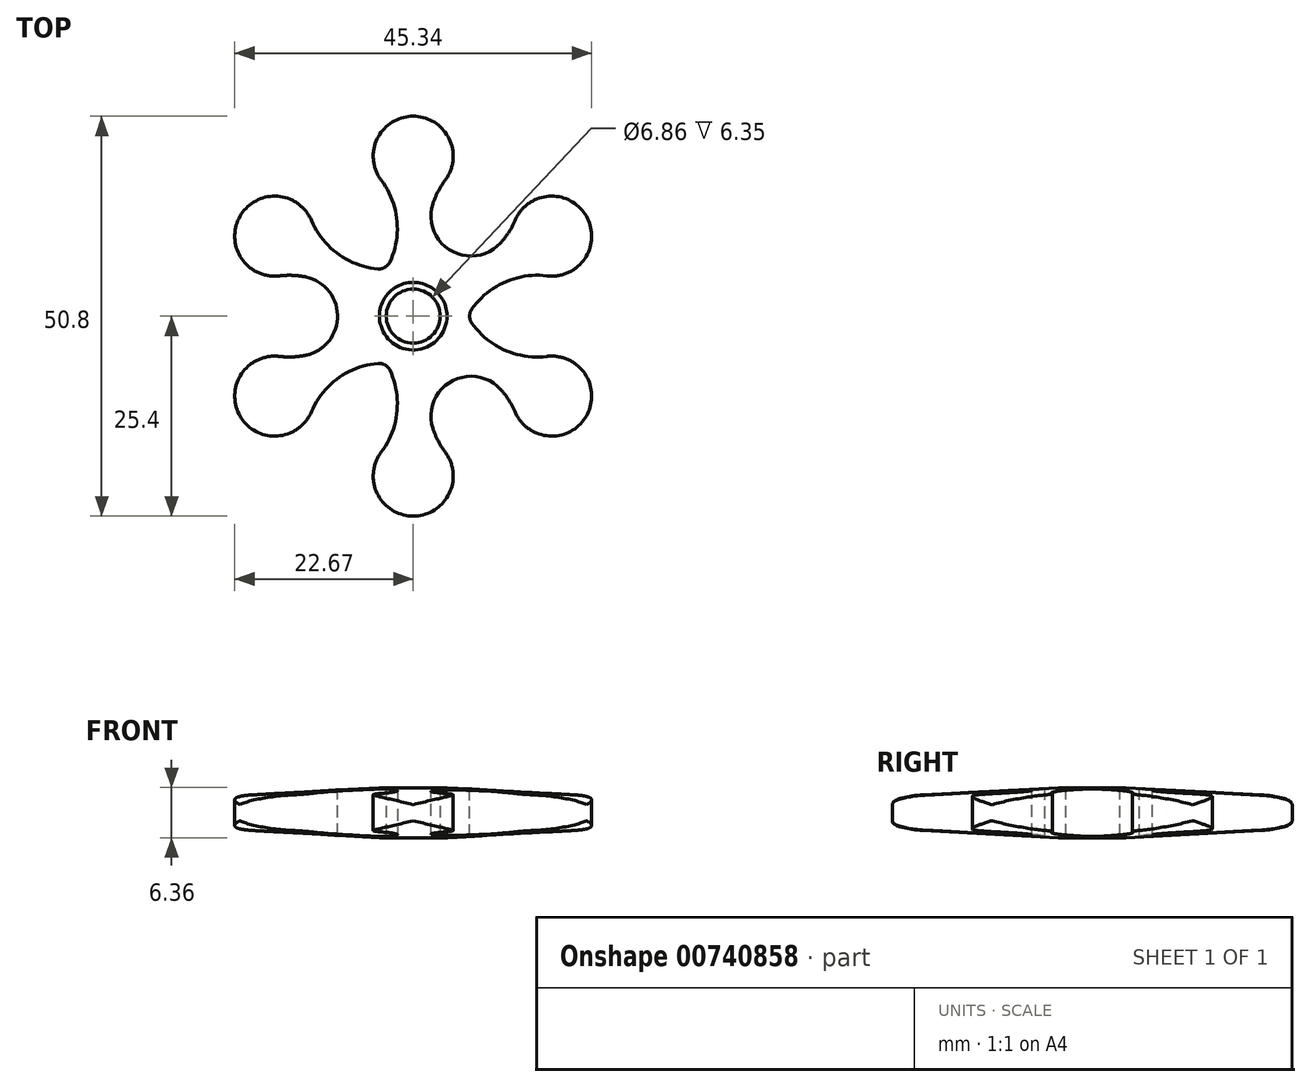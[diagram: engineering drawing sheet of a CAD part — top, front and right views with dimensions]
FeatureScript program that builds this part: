
annotation { "Feature Type Name" : "Feature", "Feature Type Description" : "" }
export const myFeature = defineFeature(function(context is Context, id is Id, definition is map)
    precondition{}
    {
        {
            var Q0;
            Q0=qCreatedBy(makeId("Top.planeOp"),FACE);
            var sketch = newSketch(context, id + "F0", { "sketchPlane" : qUnion([Q0])});
            skCircle(sketch, "E0", {"center": v(0, 0) * mm, "radius": 3.43 * mm});
            skCircle(sketch, "E1", {"center": v(0, 0) * mm, "radius": 25.4 * mm, "construction": true});
            skLineSegment(sketch, "E2", {"start": v(0, 0) * mm, "end": v(0, 25.4) * mm, "construction": true});
            skArc(sketch, "E3", {"start": v(4.06, 17.26) * mm, "mid": v(0, 25.4) * mm, "end": v(-4.06, 17.26) * mm});
            skArc(sketch, "E4", {"start": v(-4.68, 4.29) * mm, "mid": v(0, -6.35) * mm, "end": v(4.68, 4.29) * mm});
            skArc(sketch, "E5", {"start": v(-4.68, 4.29) * mm, "mid": v(-2.03, 10.66) * mm, "end": v(-4.06, 17.26) * mm});
            skPoint(sketch, "E5.first.point", {"position": v(-4.06, 17.26) * mm});
            skPoint(sketch, "E5.second.point", {"position": v(-4.68, 4.29) * mm});
            skArc(sketch, "E6", {"start": v(4.06, 17.26) * mm, "mid": v(2.03, 10.66) * mm, "end": v(4.68, 4.29) * mm});
            skPoint(sketch, "E6.first.point", {"position": v(4.06, 17.26) * mm});
            skPoint(sketch, "E6.second.point", {"position": v(4.68, 4.29) * mm});
            skArc(sketch, "E7.1.0", {"start": v(-12.92, 12.15) * mm, "mid": v(-8.22, 7.09) * mm, "end": v(-1.37, 6.2) * mm});
            skArc(sketch, "E7.1.1", {"start": v(-6.06, -1.91) * mm, "mid": v(-10.25, 3.58) * mm, "end": v(-16.98, 5.12) * mm});
            skArc(sketch, "E7.1.2", {"start": v(-12.92, 12.15) * mm, "mid": v(-22, 12.7) * mm, "end": v(-16.98, 5.12) * mm});
            skArc(sketch, "E7.2.0", {"start": v(-16.98, -5.12) * mm, "mid": v(-10.25, -3.58) * mm, "end": v(-6.06, 1.91) * mm});
            skArc(sketch, "E7.2.1", {"start": v(-1.37, -6.2) * mm, "mid": v(-8.22, -7.09) * mm, "end": v(-12.92, -12.15) * mm});
            skArc(sketch, "E7.2.2", {"start": v(-16.98, -5.12) * mm, "mid": v(-22, -12.7) * mm, "end": v(-12.92, -12.15) * mm});
            skLineSegment(sketch, "E8", {"start": v(0, 0) * mm, "end": v(-22, -12.7) * mm, "construction": true});
            skLineSegment(sketch, "E9", {"start": v(0, 0) * mm, "end": v(22, -12.7) * mm, "construction": true});
            skArc(sketch, "E10.4.3.0", {"start": v(4.68, -4.29) * mm, "mid": v(2.03, -10.66) * mm, "end": v(4.06, -17.26) * mm});
            skArc(sketch, "E10.5.3.0", {"start": v(-4.06, -17.26) * mm, "mid": v(-2.03, -10.66) * mm, "end": v(-4.68, -4.29) * mm});
            skArc(sketch, "E10.8.3.0", {"start": v(-4.06, -17.26) * mm, "mid": v(0, -25.4) * mm, "end": v(4.06, -17.26) * mm});
            skArc(sketch, "E10.4.4.0", {"start": v(6.06, 1.91) * mm, "mid": v(10.25, -3.58) * mm, "end": v(16.98, -5.12) * mm});
            skArc(sketch, "E10.5.4.0", {"start": v(12.92, -12.15) * mm, "mid": v(8.22, -7.09) * mm, "end": v(1.37, -6.2) * mm});
            skArc(sketch, "E10.8.4.0", {"start": v(12.92, -12.15) * mm, "mid": v(22, -12.7) * mm, "end": v(16.98, -5.12) * mm});
            skArc(sketch, "E10.4.5.0", {"start": v(1.37, 6.2) * mm, "mid": v(8.22, 7.09) * mm, "end": v(12.92, 12.15) * mm});
            skArc(sketch, "E10.5.5.0", {"start": v(16.98, 5.12) * mm, "mid": v(10.25, 3.58) * mm, "end": v(6.06, -1.91) * mm});
            skArc(sketch, "E10.8.5.0", {"start": v(16.98, 5.12) * mm, "mid": v(22, 12.7) * mm, "end": v(12.92, 12.15) * mm});
            skSolve(sketch);
        }
        {
            var Q0;
            {var subQ0=sQuery(id+"F0.wireOp",EDGE,"E7.1.0");Q0=makeQuery(id+"F0.imprint","IMPRINT",FACE,{"disambiguationData":[TD([[makeQuery(id+"F0.imprint","IMPRINT",EDGE,{"derivedFrom":subQ0}),-1.0]])]});}
            var Q1;
            {var subQ0=sQuery(id+"F0.wireOp",EDGE,"E10.8.5.0");Q1=makeQuery(id+"F0.imprint","IMPRINT",FACE,{"disambiguationData":[TD([[makeQuery(id+"F0.imprint","IMPRINT",EDGE,{"derivedFrom":subQ0}),1.0]])]});}
            var Q2;
            {var subQ0=sQuery(id+"F0.wireOp",EDGE,"E10.8.4.0");Q2=makeQuery(id+"F0.imprint","IMPRINT",FACE,{"disambiguationData":[TD([[makeQuery(id+"F0.imprint","IMPRINT",EDGE,{"derivedFrom":subQ0}),1.0]])]});}
            var Q3;
            {var subQ0=sQuery(id+"F0.wireOp",EDGE,"E10.8.3.0");Q3=makeQuery(id+"F0.imprint","IMPRINT",FACE,{"disambiguationData":[TD([[makeQuery(id+"F0.imprint","IMPRINT",EDGE,{"derivedFrom":subQ0}),1.0]])]});}
            var Q4;
            {var subQ0=sQuery(id+"F0.wireOp",EDGE,"E7.2.2");Q4=makeQuery(id+"F0.imprint","IMPRINT",FACE,{"disambiguationData":[TD([[makeQuery(id+"F0.imprint","IMPRINT",EDGE,{"derivedFrom":subQ0}),1.0]])]});}
            var Q5;
            {var subQ0=sQuery(id+"F0.wireOp",EDGE,"E7.1.1");var subQ1=sQuery(id+"F0.wireOp",EDGE,"E4");var subQ2=makeQuery(id+"F0.imprint","INTERSECT",VERTEX,{"derivedFrom":[subQ1,subQ0]});Q5=makeQuery(id+"F0.imprint","IMPRINT",FACE,{"disambiguationData":[TD([[makeQuery(id+"F0.imprint","IMPRINT",EDGE,{"disambiguationData":[TD([[subQ2,1.0]])],"derivedFrom":subQ1}),-1.0]])]});}
            var Q6;
            Q6=makeQuery(id+"F0.imprint","IMPRINT",FACE,{"disambiguationData":[TD([[makeQuery(id+"F0.imprint","IMPRINT",EDGE,{"derivedFrom":sQuery(id+"F0.wireOp",EDGE,"E0")}),-1.0]])]});
            var Q7;
            {var subQ0=sQuery(id+"F0.wireOp",EDGE,"E7.2.1");var subQ1=sQuery(id+"F0.wireOp",EDGE,"E4");var subQ2=makeQuery(id+"F0.imprint","INTERSECT",VERTEX,{"derivedFrom":[subQ1,subQ0]});Q7=makeQuery(id+"F0.imprint","IMPRINT",FACE,{"disambiguationData":[TD([[makeQuery(id+"F0.imprint","IMPRINT",EDGE,{"disambiguationData":[TD([[subQ2,1.0]])],"derivedFrom":subQ1}),-1.0]])]});}
            var Q8;
            {var subQ0=sQuery(id+"F0.wireOp",EDGE,"E10.4.3.0");var subQ1=sQuery(id+"F0.wireOp",EDGE,"E4");var subQ2=makeQuery(id+"F0.imprint","INTERSECT",VERTEX,{"derivedFrom":[subQ1,subQ0]});Q8=makeQuery(id+"F0.imprint","IMPRINT",FACE,{"disambiguationData":[TD([[makeQuery(id+"F0.imprint","IMPRINT",EDGE,{"disambiguationData":[TD([[subQ2,1.0]])],"derivedFrom":subQ1}),-1.0]])]});}
            var Q9;
            {var subQ0=sQuery(id+"F0.wireOp",EDGE,"E10.4.4.0");var subQ1=sQuery(id+"F0.wireOp",EDGE,"E4");var subQ2=makeQuery(id+"F0.imprint","INTERSECT",VERTEX,{"derivedFrom":[subQ1,subQ0]});Q9=makeQuery(id+"F0.imprint","IMPRINT",FACE,{"disambiguationData":[TD([[makeQuery(id+"F0.imprint","IMPRINT",EDGE,{"disambiguationData":[TD([[subQ2,1.0]])],"derivedFrom":subQ1}),-1.0]])]});}
            extrude(context, id + "F1", {"entities" : qUnion([Q0, Q1, Q2, Q3, Q4, Q5, Q6, Q7, Q8, Q9]), "endBound" : BoundingType.SYMMETRIC, "depth" : 6.35 * mm, "offsetDistance" : 25.4 * mm});
        }
        {
            var Q0;
            Q0=qCreatedBy(makeId("Right.planeOp"),FACE);
            var sketch = newSketch(context, id + "F2", { "sketchPlane" : qUnion([Q0])});
            skLineSegment(sketch, "E11", {"start": v(0, 0) * mm, "end": v(25.4, 0) * mm, "construction": true});
            skLineSegment(sketch, "E12", {"start": v(25.4, 3.18) * mm, "end": v(25.4, -3.18) * mm, "construction": true});
            skLineSegment(sketch, "E13.0", {"start": v(17.26, 3.18) * mm, "end": v(17.26, -3.17) * mm, "construction": true});
            skLineSegment(sketch, "E14.0", {"start": v(4.29, 3.18) * mm, "end": v(4.29, -3.17) * mm, "construction": true});
            skLineSegment(sketch, "E15", {"start": v(4.29, -3.17) * mm, "end": v(25.4, -2.03) * mm, "construction": true});
            skPoint(sketch, "E16.first.point", {"position": v(21.6, -2.24) * mm});
            skPoint(sketch, "E16.second.point", {"position": v(25.4, -1.02) * mm});
            skLineSegment(sketch, "E17", {"start": v(25.4, -1.02) * mm, "end": v(25.4, -3.18) * mm});
            skLineSegment(sketch, "E18", {"start": v(4.29, -3.17) * mm, "end": v(21.6, -2.24) * mm});
            skLineSegment(sketch, "E19", {"start": v(25.4, -3.18) * mm, "end": v(4.29, -3.17) * mm});
            skFitSpline(sketch, "E20", {"points": [v(25.4, -1.02) * mm, v(21.6, -2.24) * mm], "startDerivative": vector(0, -3.05) * mm, "endDerivative": vector(-0.76, -0.04) * mm});
            skLineSegment(sketch, "E21.MirrorCS", {"start": v(4.29, 3.17) * mm, "end": v(21.6, 2.24) * mm});
            skPoint(sketch, "E22.MirrorP", {"position": v(21.6, 2.24) * mm});
            skLineSegment(sketch, "E23.MirrorCS", {"start": v(25.4, 3.18) * mm, "end": v(4.29, 3.17) * mm});
            skLineSegment(sketch, "E24.MirrorCS", {"start": v(25.4, 1.02) * mm, "end": v(25.4, 3.18) * mm});
            skPoint(sketch, "E25.MirrorP", {"position": v(25.4, 1.02) * mm});
            skFitSpline(sketch, "E26.MirrorCS", {"points": [v(25.4, 1.02) * mm, v(21.6, 2.24) * mm], "startDerivative": vector(0, 3.05) * mm, "endDerivative": vector(-0.76, 0.04) * mm});
            skSolve(sketch);
        }
        {
            var Q0;
            Q0 = qSketchRegion(id + "F2", true);
            var Q1;
            Q1=makeQuery(id+"F1.opExtrude","SWEPT_FACE",FACE,{"disambiguationData":[OSD([sQuery(id+"F0.wireOp",EDGE,"E0")])]});
            revolve(context, id + "F3", {"operationType" : NewBodyOperationType.REMOVE, "surfaceOperationType" : NewSurfaceOperationType.NEW, "entities" : qUnion([Q0]), "axis" : qUnion([Q1]), "revolveType" : RevolveType.FULL, "oppositeDirection" : true});
        }
        {
            var Q0;
            Q0=makeQuery(id+"F1.opExtrude","SWEPT_EDGE",EDGE,{"disambiguationData":[OSD([sQuery(id+"F0.wireOp",EDGE,"E6"),sQuery(id+"F0.wireOp",EDGE,"E10.4.5.0")])]});
            var Q1;
            Q1=makeQuery(id+"F1.opExtrude","SWEPT_EDGE",EDGE,{"disambiguationData":[OSD([sQuery(id+"F0.wireOp",EDGE,"E10.4.3.0"),sQuery(id+"F0.wireOp",EDGE,"E10.5.4.0")])]});
            var Q2;
            Q2=makeQuery(id+"F1.opExtrude","SWEPT_EDGE",EDGE,{"disambiguationData":[OSD([sQuery(id+"F0.wireOp",EDGE,"E7.1.1"),sQuery(id+"F0.wireOp",EDGE,"E7.2.0")])]});
            fillet(context, id + "F4", {"entities" : qUnion([Q0, Q1, Q2]), "radius" : 5.08 * mm, "tangentPropagation" : true, "allowEdgeOverflow" : false});
        }
        {
            var Q0;
            Q0=makeQuery(id+"F1.opExtrude","SWEPT_EDGE",EDGE,{"disambiguationData":[OSD([sQuery(id+"F0.wireOp",EDGE,"E7.2.1"),sQuery(id+"F0.wireOp",EDGE,"E10.5.3.0")])]});
            var Q1;
            Q1=makeQuery(id+"F1.opExtrude","SWEPT_EDGE",EDGE,{"disambiguationData":[OSD([sQuery(id+"F0.wireOp",EDGE,"E5"),sQuery(id+"F0.wireOp",EDGE,"E7.1.0")])]});
            var Q2;
            Q2=makeQuery(id+"F1.opExtrude","SWEPT_EDGE",EDGE,{"disambiguationData":[OSD([sQuery(id+"F0.wireOp",EDGE,"E10.4.4.0"),sQuery(id+"F0.wireOp",EDGE,"E10.5.5.0")])]});
            fillet(context, id + "F5", {"entities" : qUnion([Q0, Q1, Q2]), "radius" : 1.52 * mm, "tangentPropagation" : true, "allowEdgeOverflow" : false});
        }
    });
